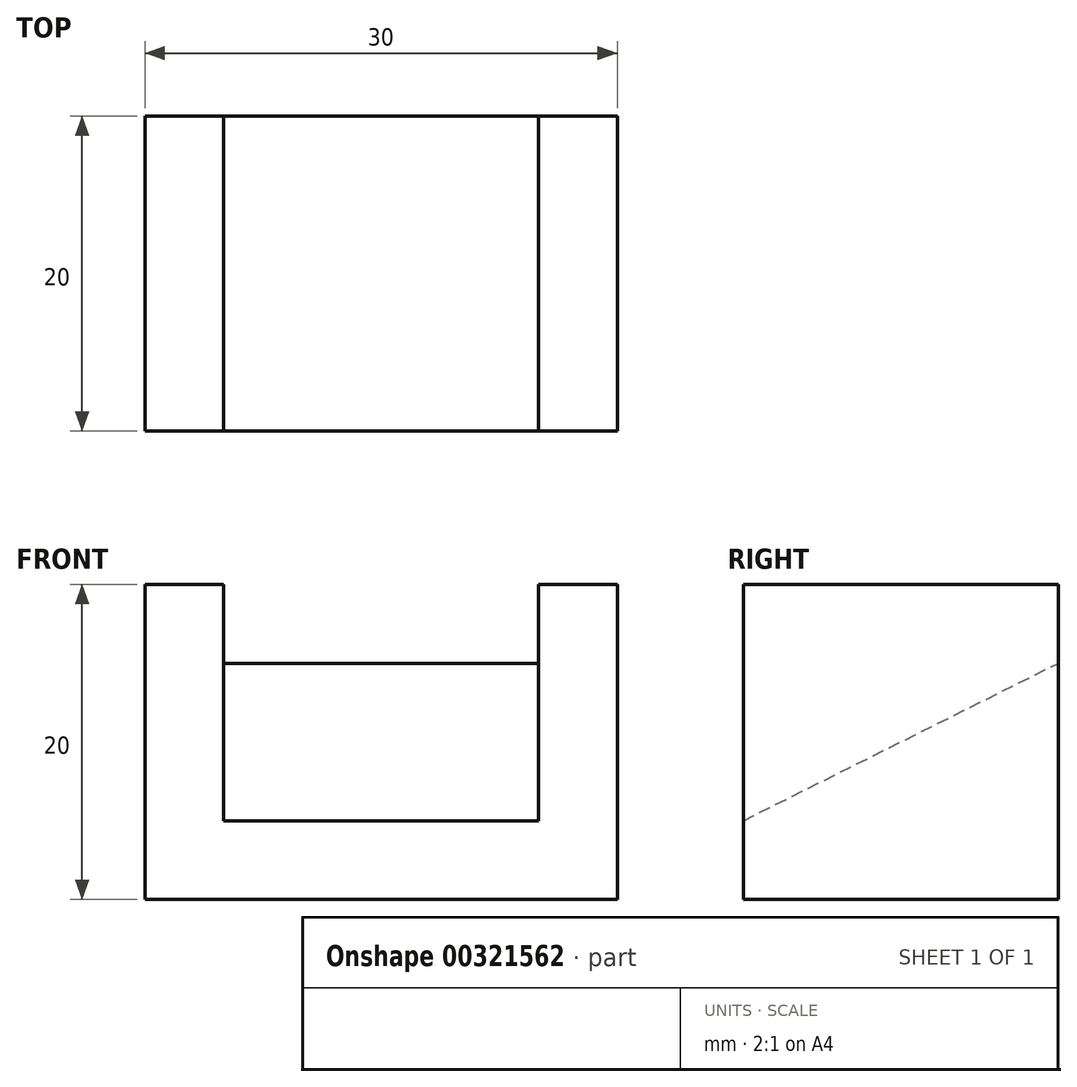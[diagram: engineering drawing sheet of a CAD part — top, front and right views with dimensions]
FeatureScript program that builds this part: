
annotation { "Feature Type Name" : "Feature", "Feature Type Description" : "" }
export const myFeature = defineFeature(function(context is Context, id is Id, definition is map)
    precondition{}
    {
        {
            var Q0;
            Q0=qCreatedBy(makeId("Front.planeOp"),FACE);
            var sketch = newSketch(context, id + "F0", { "sketchPlane" : qUnion([Q0])});
            skLineSegment(sketch, "E0", {"start": v(0, 0) * mm, "end": v(30, 0) * mm});
            skLineSegment(sketch, "E1", {"start": v(30, 0) * mm, "end": v(30, 20) * mm});
            skLineSegment(sketch, "E2", {"start": v(30, 20) * mm, "end": v(25, 20) * mm});
            skLineSegment(sketch, "E3", {"start": v(25, 20) * mm, "end": v(25, 5) * mm});
            skLineSegment(sketch, "E4", {"start": v(25, 5) * mm, "end": v(5, 5) * mm});
            skLineSegment(sketch, "E5", {"start": v(5, 5) * mm, "end": v(5, 20) * mm});
            skLineSegment(sketch, "E6", {"start": v(5, 20) * mm, "end": v(0, 20) * mm});
            skLineSegment(sketch, "E7", {"start": v(0, 20) * mm, "end": v(0, 0) * mm});
            skSolve(sketch);
        }
        {
            var Q0;
            Q0 = qSketchRegion(id + "F0", true);
            extrude(context, id + "F1", {"entities" : qUnion([Q0]), "depth" : 20 * mm});
        }
        {
            var Q0;
            Q0=makeQuery(id+"F1.opExtrude","SWEPT_FACE",FACE,{"disambiguationData":[OSD([sQuery(id+"F0.wireOp",EDGE,"E1")])]});
            var sketch = newSketch(context, id + "F2", { "sketchPlane" : qUnion([Q0])});
            skLineSegment(sketch, "E8", {"start": v(-20, 0) * mm, "end": v(-20, 5) * mm});
            skLineSegment(sketch, "E9", {"start": v(-20, 5) * mm, "end": v(0, 15) * mm});
            skLineSegment(sketch, "E10", {"start": v(0, 15) * mm, "end": v(0, 0) * mm});
            skLineSegment(sketch, "E11", {"start": v(0, 0) * mm, "end": v(-20, 0) * mm});
            skSolve(sketch);
        }
        {
            var Q0;
            Q0 = qSketchRegion(id + "F2", true);
            extrude(context, id + "F3", {"entities" : qUnion([Q0]), "operationType" : NewBodyOperationType.ADD, "endBound" : BoundingType.UP_TO_NEXT, "oppositeDirection" : true, "depth" : 30.5 * mm});
        }
    });
